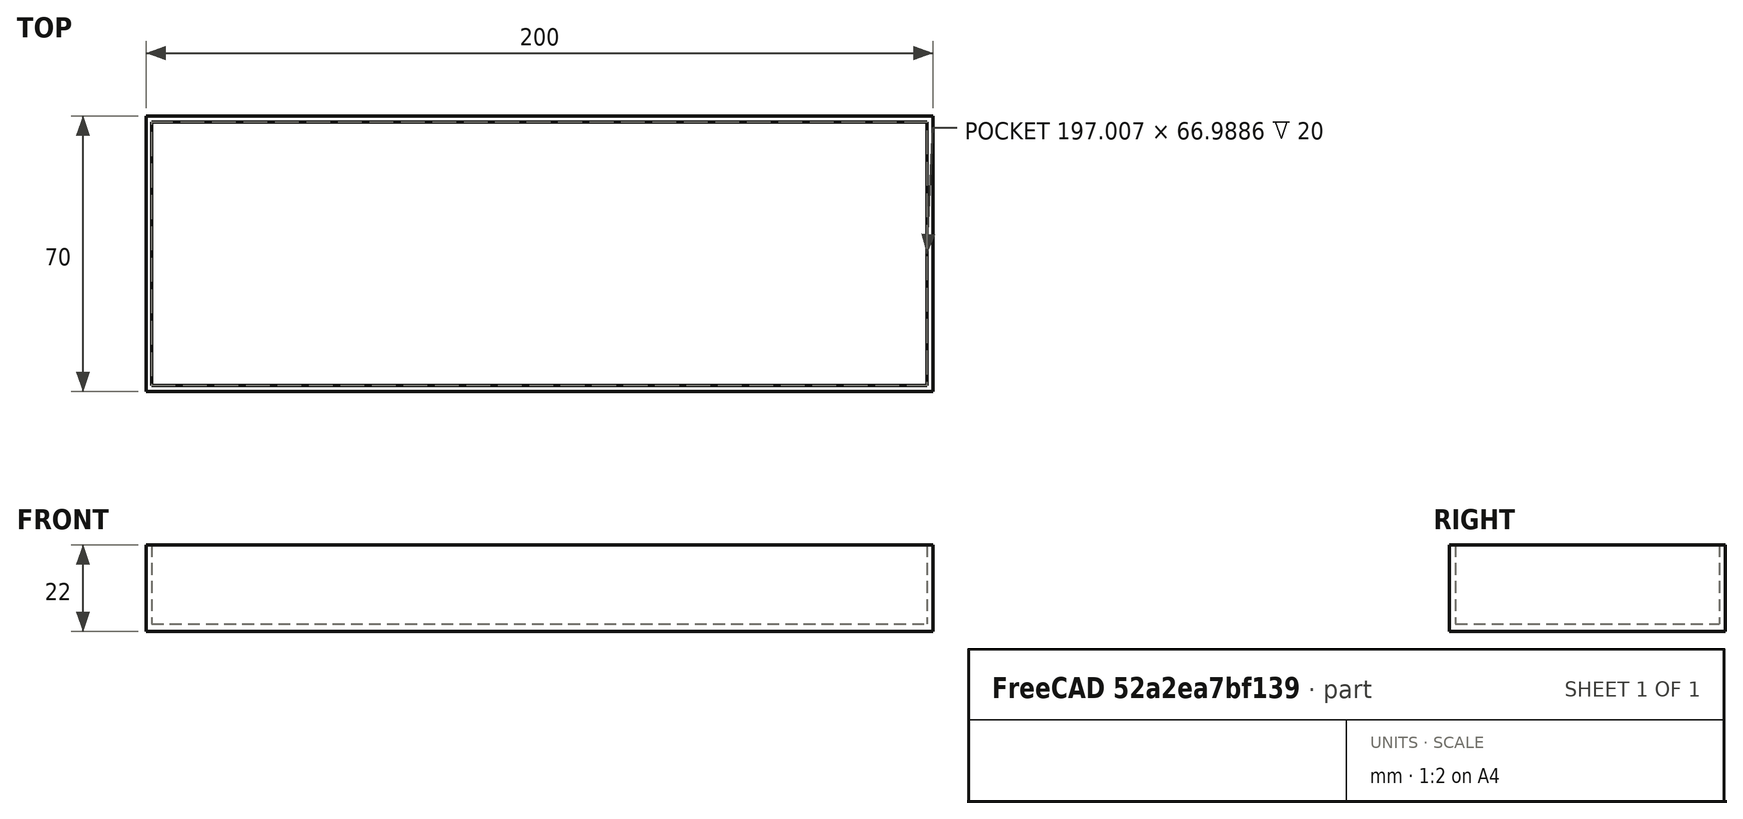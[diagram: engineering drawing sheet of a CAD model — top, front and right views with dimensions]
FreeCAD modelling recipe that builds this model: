
FCSTD DOCUMENT  (FreeCAD 0.17R13522 (Git))
Label: Casing
License: All rights reserved
LicenseURL: http://en.wikipedia.org/wiki/All_rights_reserved
objects: Sketcher::SketchObject×2, PartDesign::Body×1, PartDesign::Pad×1, PartDesign::Pocket×1
note: 7 computed .brp shape members not serialized (recipe doc carries the construction recipe); baked Part::Feature solids carry a one-line shape summary decoded from their .brp

FEATURE [PartDesign::Body] Body
  Group = -> [Sketch,Pad,Sketch001,Pocket]
  Origin = -> Origin
  Tip = -> Pocket
FEATURE [Sketcher::SketchObject] Sketch
  MapMode = 2
  Placement = pos=(0,0,45) rot=(0,0,1;0rad)
  Support = -> [Sketch001]
  sketch-geometry (4):
    g0: LineSegment StartX=0 StartY=0 StartZ=0 EndX=200 EndY=0 EndZ=0
    g1: LineSegment StartX=200 StartY=0 StartZ=0 EndX=200 EndY=70 EndZ=0
    g2: LineSegment StartX=200 StartY=70 StartZ=0 EndX=0 EndY=70 EndZ=0
    g3: LineSegment StartX=0 StartY=70 StartZ=0 EndX=0 EndY=0 EndZ=0
  constraints (11):
    c: Coincident(g0,g1)
    c: Coincident(g1,g2)
    c: Coincident(g2,g3)
    c: Coincident(g3,g0)
    c: Horizontal(g0)
    c: Horizontal(g2)
    c: Vertical(g1)
    c: Vertical(g3)
    c: Coincident(g0,g-1)
    c: DistanceX(g0,g0) = 200
    c: DistanceY(g1,g1) = 70
FEATURE [PartDesign::Pad] Pad
  Length = 22
  Length2 = 100
  Placement = pos=(0,0,45) rot=(0,0,1;0rad)
  Profile = -> Sketch
  Reversed = true
  Type = 0
FEATURE [Sketcher::SketchObject] Sketch001
  MapMode = 5
  Placement = pos=(0,0,45) rot=(0,0,1;0rad)
  Support = -> [Pad]
  sketch-geometry (4):
    g0: LineSegment StartX=1.47451 StartY=1.51562 StartZ=0 EndX=198.481 EndY=1.51562 EndZ=0
    g1: LineSegment StartX=198.481 StartY=1.51562 StartZ=0 EndX=198.481 EndY=68.5042 EndZ=0
    g2: LineSegment StartX=198.481 StartY=68.5042 StartZ=0 EndX=1.47451 EndY=68.5042 EndZ=0
    g3: LineSegment StartX=1.47451 StartY=68.5042 StartZ=0 EndX=1.47451 EndY=1.51562 EndZ=0
  constraints (8):
    c: Coincident(g0,g1)
    c: Coincident(g1,g2)
    c: Coincident(g2,g3)
    c: Coincident(g3,g0)
    c: Horizontal(g0)
    c: Horizontal(g2)
    c: Vertical(g1)
    c: Vertical(g3)
FEATURE [PartDesign::Pocket] Pocket
  BaseFeature = -> Pad
  Length = 20
  Length2 = 100
  Placement = pos=(0,0,45) rot=(0,0,1;0rad)
  Profile = -> Sketch001
  Type = 0
